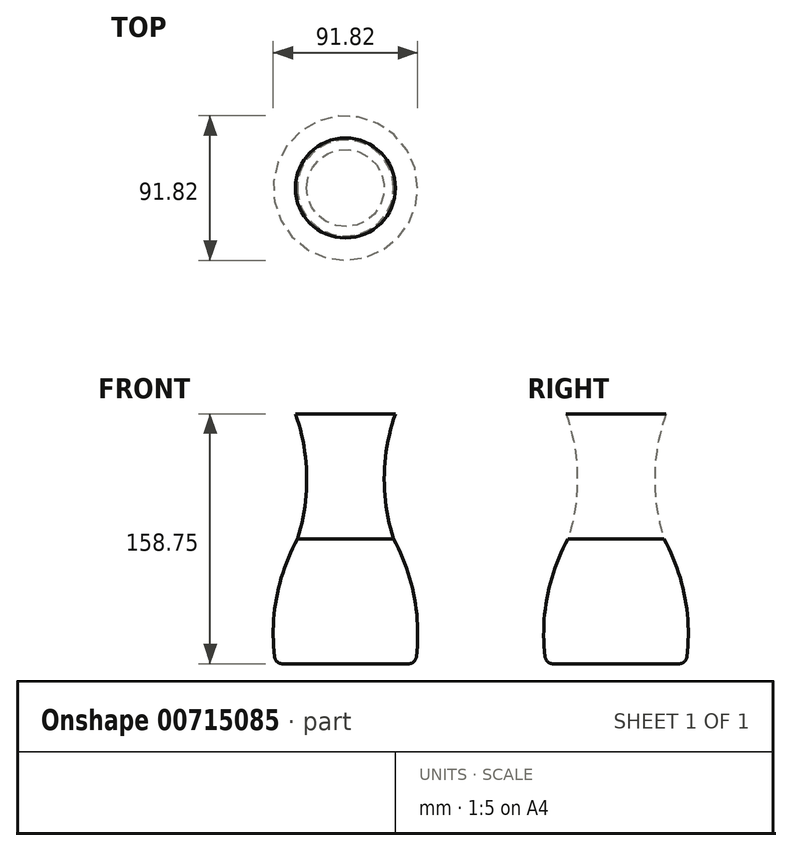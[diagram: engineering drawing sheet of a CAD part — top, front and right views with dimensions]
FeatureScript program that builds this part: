
annotation { "Feature Type Name" : "Feature", "Feature Type Description" : "" }
export const myFeature = defineFeature(function(context is Context, id is Id, definition is map)
    precondition{}
    {
        {
            var Q0;
            Q0=qCreatedBy(makeId("Front.planeOp"),FACE);
            var sketch = newSketch(context, id + "F0", { "sketchPlane" : qUnion([Q0])});
            skLineSegment(sketch, "E0", {"start": v(0, 0) * mm, "end": v(0, 158.75) * mm});
            skLineSegment(sketch, "E1", {"start": v(0, 0) * mm, "end": v(-44.45, 0) * mm});
            skLineSegment(sketch, "E2", {"start": v(0, 158.75) * mm, "end": v(-31.75, 158.75) * mm});
            skPoint(sketch, "E3", {"position": v(0, 79.38) * mm});
            skLineSegment(sketch, "E4", {"start": v(0, 79.38) * mm, "end": v(-30.48, 79.38) * mm});
            skArc(sketch, "E5", {"start": v(-30.48, 79.38) * mm, "mid": v(-24.63, 119.17) * mm, "end": v(-31.75, 158.75) * mm});
            skArc(sketch, "E6", {"start": v(-30.48, 79.37) * mm, "mid": v(-44, 40.84) * mm, "end": v(-44.45, 0) * mm});
            skLineSegment(sketch, "E7", {"start": v(0, 158.75) * mm, "end": v(-30.99, 158.75) * mm});
            skLineSegment(sketch, "E8", {"start": v(0, 79.38) * mm, "end": v(-29.72, 79.38) * mm});
            skLineSegment(sketch, "E9", {"start": v(0, 0) * mm, "end": v(-43.69, 0) * mm});
            skArc(sketch, "E10", {"start": v(-29.72, 79.37) * mm, "mid": v(-43.24, 40.84) * mm, "end": v(-43.69, 0) * mm});
            skArc(sketch, "E11", {"start": v(-29.72, 79.38) * mm, "mid": v(-23.87, 119.17) * mm, "end": v(-30.99, 158.75) * mm});
            skSolve(sketch);
        }
        {
            var Q0;
            {var subQ0=sQuery(id+"F0.wireOp",EDGE,"E2");Q0=makeQuery(id+"F0.imprint","IMPRINT",FACE,{"disambiguationData":[TD([[makeQuery(id+"F0.imprint","IMPRINT",EDGE,{"derivedFrom":subQ0}),1.0]])]});}
            var Q1;
            {var subQ0=sQuery(id+"F0.wireOp",EDGE,"E1");Q1=makeQuery(id+"F0.imprint","IMPRINT",FACE,{"disambiguationData":[TD([[makeQuery(id+"F0.imprint","IMPRINT",EDGE,{"derivedFrom":subQ0}),-1.0]])]});}
            var Q2;
            Q2=sQuery(id+"F0.wireOp",EDGE,"E0");
            revolve(context, id + "F1", {"surfaceOperationType" : NewSurfaceOperationType.NEW, "entities" : qUnion([Q0, Q1]), "axis" : qUnion([Q2]), "revolveType" : RevolveType.FULL});
        }
        {
            var Q0;
            Q0=makeQuery(id+"F1.opRevolve","SWEPT_EDGE",EDGE,{"disambiguationData":[OSD([sQuery(id+"F0.wireOp",EDGE,"E1"),sQuery(id+"F0.wireOp",EDGE,"E6")])]});
            fillet(context, id + "F2", {"entities" : qUnion([Q0]), "radius" : 5.08 * mm, "tangentPropagation" : true, "allowEdgeOverflow" : false});
        }
    });
